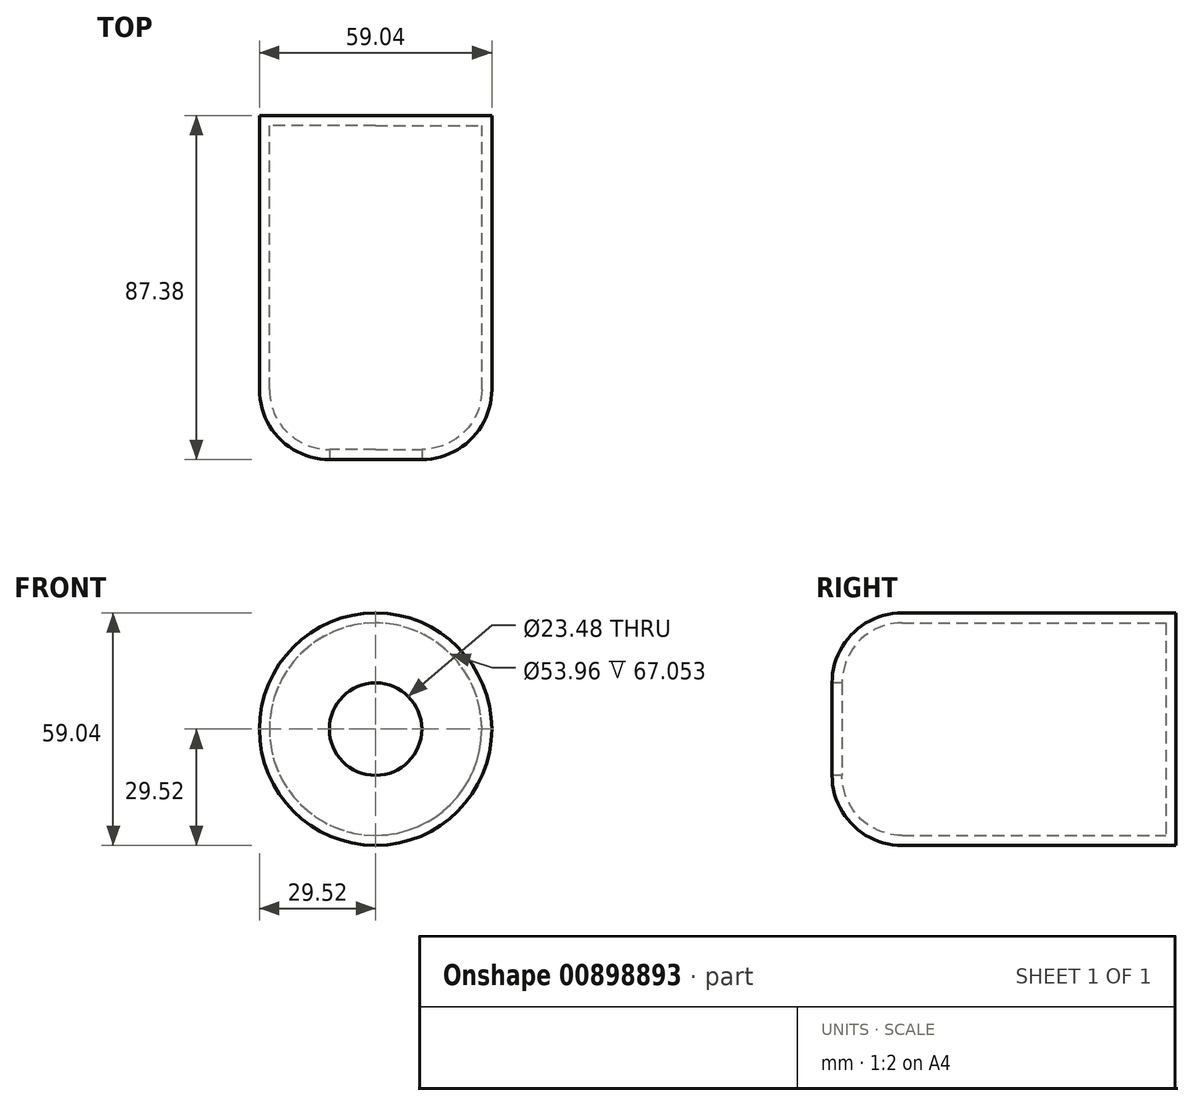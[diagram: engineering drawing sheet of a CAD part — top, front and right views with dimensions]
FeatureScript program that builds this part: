
annotation { "Feature Type Name" : "Feature", "Feature Type Description" : "" }
export const myFeature = defineFeature(function(context is Context, id is Id, definition is map)
    precondition{}
    {
        {
            var Q0;
            Q0=qCreatedBy(makeId("Front.planeOp"),FACE);
            var sketch = newSketch(context, id + "F0", { "sketchPlane" : qUnion([Q0])});
            skCircle(sketch, "E0", {"center": v(0, 0) * mm, "radius": 29.52 * mm});
            skSolve(sketch);
        }
        {
            var Q0;
            Q0=makeQuery(id+"F0.imprint","IMPRINT",FACE,{"disambiguationData":[TD([[makeQuery(id+"F0.imprint","IMPRINT",EDGE,{"derivedFrom":sQuery(id+"F0.wireOp",EDGE,"E0")}),1.0]])]});
            extrude(context, id + "F1", {"entities" : qUnion([Q0]), "depth" : 87.38 * mm, "offsetDistance" : 25.4 * mm});
        }
        {
            var Q0;
            Q0=makeQuery(id+"F1.opExtrude","CAP_FACE",FACE,{"disambiguationData":[OSD([sQuery(id+"F0.wireOp",EDGE,"E0")])],"isStart":false});
            fillet(context, id + "F2", {"entities" : qUnion([Q0]), "radius" : 17.78 * mm, "tangentPropagation" : true, "allowEdgeOverflow" : false});
        }
        {
            var Q0;
            Q0=makeQuery(id+"F1.opExtrude","CAP_FACE",FACE,{"disambiguationData":[OSD([sQuery(id+"F0.wireOp",EDGE,"E0")])],"isStart":false});
            shell(context, id + "F3", {"entities" : qUnion([Q0]), "thickness" : 2.54 * mm});
        }
    });
